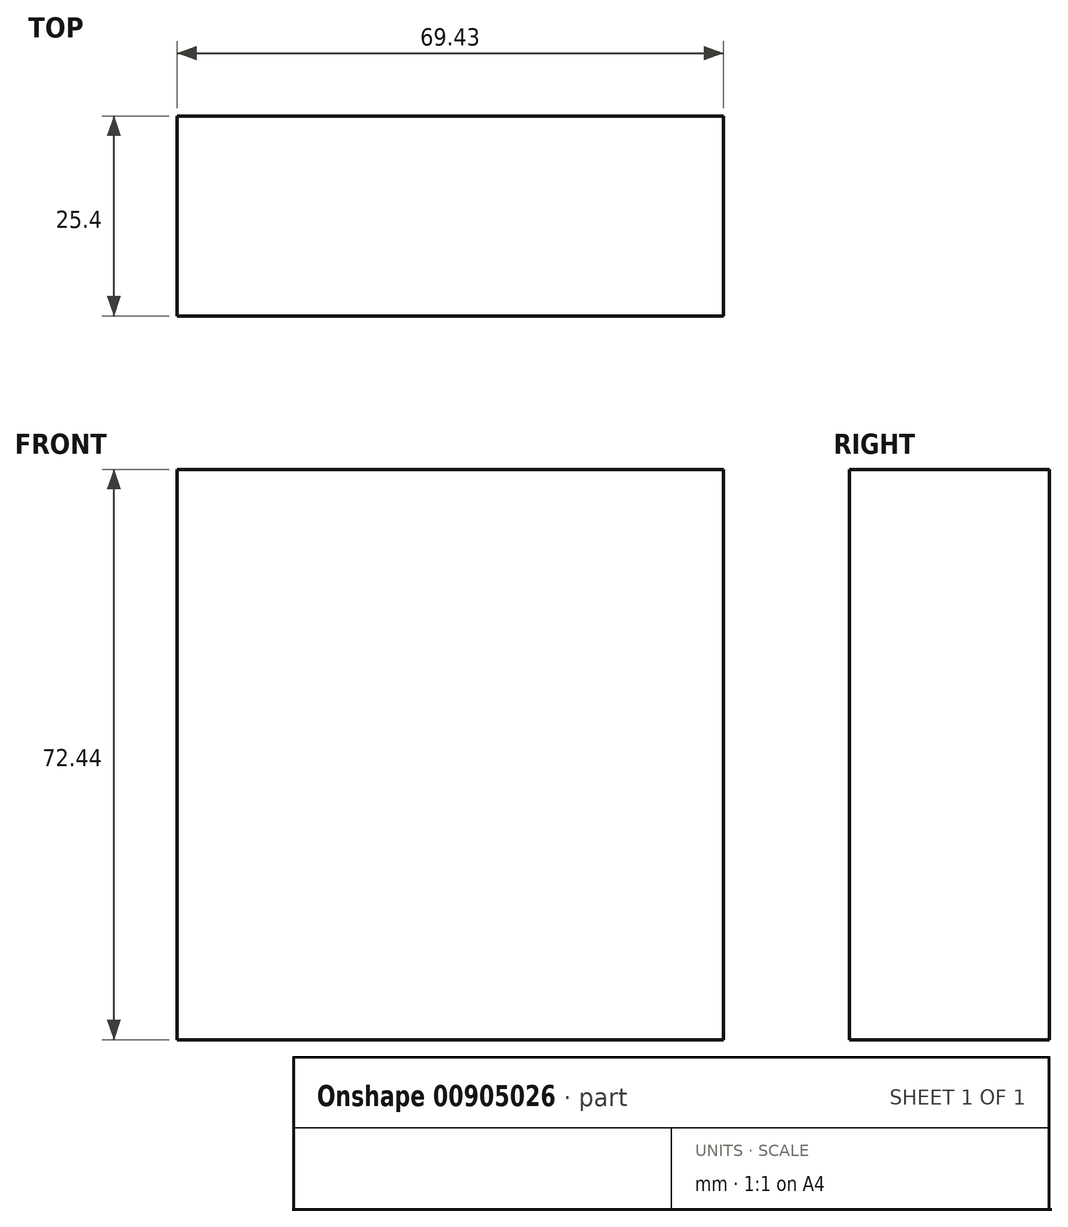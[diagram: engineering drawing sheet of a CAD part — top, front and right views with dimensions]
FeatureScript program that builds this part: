
annotation { "Feature Type Name" : "Feature", "Feature Type Description" : "" }
export const myFeature = defineFeature(function(context is Context, id is Id, definition is map)
    precondition{}
    {
        {
            var Q0;
            Q0=qCreatedBy(makeId("Front.planeOp"),FACE);
            var sketch = newSketch(context, id + "F0", { "sketchPlane" : qUnion([Q0])});
            skLineSegment(sketch, "E0.bottom", {"start": v(0, 0) * mm, "end": v(69.43, 0) * mm});
            skLineSegment(sketch, "E0.top", {"start": v(0, 72.44) * mm, "end": v(69.43, 72.44) * mm});
            skLineSegment(sketch, "E0.left", {"start": v(0, 0) * mm, "end": v(0, 72.44) * mm});
            skLineSegment(sketch, "E0.right", {"start": v(69.43, 0) * mm, "end": v(69.43, 72.44) * mm});
            skSolve(sketch);
        }
        {
            var Q0;
            Q0=makeQuery(id+"F0.imprint","IMPRINT",FACE,{"disambiguationData":[TD([[makeQuery(id+"F0.imprint","IMPRINT",EDGE,{"derivedFrom":sQuery(id+"F0.wireOp",EDGE,"E0.bottom")}),1.0]])]});
            extrude(context, id + "F1", {"entities" : qUnion([Q0]), "depth" : 25.4 * mm, "offsetDistance" : 25.4 * mm});
        }
    });
